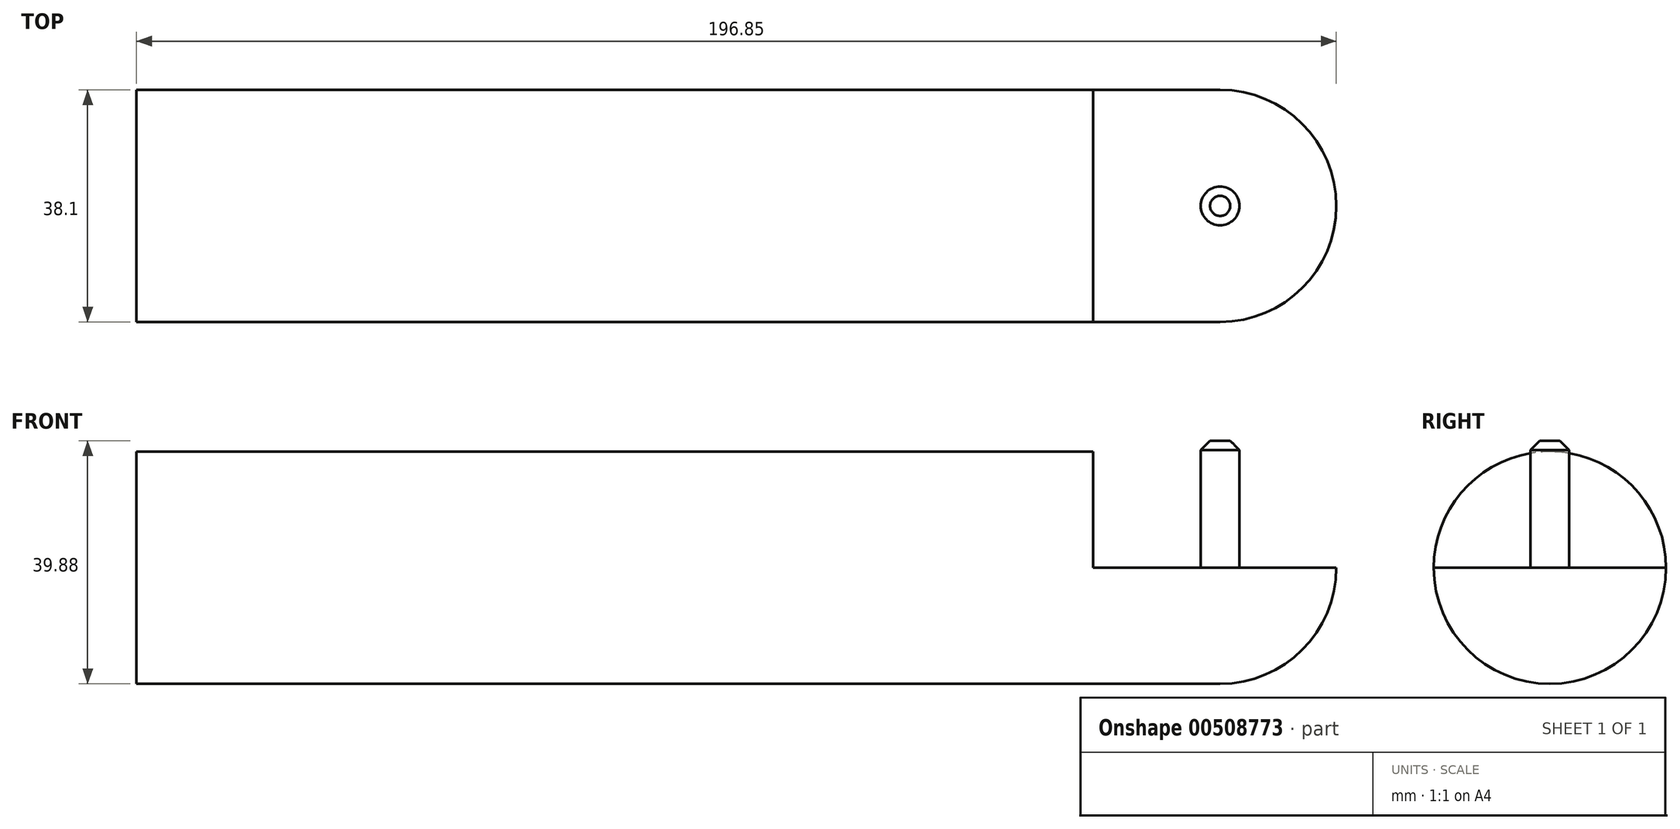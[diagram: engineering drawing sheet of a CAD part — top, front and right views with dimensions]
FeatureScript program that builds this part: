
annotation { "Feature Type Name" : "Feature", "Feature Type Description" : "" }
export const myFeature = defineFeature(function(context is Context, id is Id, definition is map)
    precondition{}
    {
        {
            var Q0;
            Q0=qCreatedBy(makeId("Top.planeOp"),FACE);
            var sketch = newSketch(context, id + "F0", { "sketchPlane" : qUnion([Q0])});
            skLineSegment(sketch, "E0.0", {"start": v(0, -19.05) * mm, "end": v(-177.8, -19.05) * mm});
            skLineSegment(sketch, "E1.0", {"start": v(0, 19.05) * mm, "end": v(-177.8, 19.05) * mm});
            skLineSegment(sketch, "E2", {"start": v(-177.8, 19.05) * mm, "end": v(-177.8, 0) * mm});
            skLineSegment(sketch, "E3", {"start": v(-177.8, -19.05) * mm, "end": v(-177.8, 0) * mm});
            skArc(sketch, "E4", {"start": v(0, 19.05) * mm, "mid": v(19.05, 0) * mm, "end": v(0, -19.05) * mm});
            skLineSegment(sketch, "E5", {"start": v(-177.8, 0) * mm, "end": v(19.05, 0) * mm});
            skSolve(sketch);
        }
        {
            var Q0;
            {var subQ0=sQuery(id+"F0.wireOp",EDGE,"E1.0");Q0=makeQuery(id+"F0.imprint","IMPRINT",FACE,{"disambiguationData":[TD([[makeQuery(id+"F0.imprint","IMPRINT",EDGE,{"derivedFrom":subQ0}),1.0]])]});}
            var Q1;
            Q1=sQuery(id+"F0.wireOp",EDGE,"E5");
            revolve(context, id + "F1", {"entities" : qUnion([Q0]), "axis" : qUnion([Q1]), "revolveType" : RevolveType.FULL});
        }
        {
            var Q0;
            Q0=qCreatedBy(makeId("Top.planeOp"),FACE);
            var sketch = newSketch(context, id + "F2", { "sketchPlane" : qUnion([Q0])});
            skArc(sketch, "E6", {"start": v(0, -19.05) * mm, "mid": v(19.05, 0) * mm, "end": v(0, 19.05) * mm});
            skLineSegment(sketch, "E7", {"start": v(-177.8, 19.05) * mm, "end": v(0, 19.05) * mm});
            skLineSegment(sketch, "E8", {"start": v(0, 0) * mm, "end": v(-20.83, 0) * mm});
            skLineSegment(sketch, "E9", {"start": v(-20.83, 0) * mm, "end": v(-20.83, 19.05) * mm});
            skLineSegment(sketch, "E10", {"start": v(-20.83, 0) * mm, "end": v(-20.83, -19.05) * mm});
            skLineSegment(sketch, "E11", {"start": v(0, -19.05) * mm, "end": v(-177.8, -19.05) * mm});
            skSolve(sketch);
        }
        {
            var Q0;
            Q0=qSketchRegion(id+"F2",true);
            extrude(context, id + "F3", {"entities" : qUnion([Q0]), "operationType" : NewBodyOperationType.REMOVE, "depth" : 25.4 * mm});
        }
        {
            var Q0;
            Q0=makeQuery(id+"F3.boolean.opBoolean","COPY",FACE,{"derivedFrom":makeQuery(id+"F3.opExtrude","CAP_FACE",FACE,{"disambiguationData":[OSD([sQuery(id+"F2.wireOp",EDGE,"E6"),sQuery(id+"F2.wireOp",EDGE,"E7"),sQuery(id+"F2.wireOp",EDGE,"E9"),sQuery(id+"F2.wireOp",EDGE,"E10"),sQuery(id+"F2.wireOp",EDGE,"E11")])],"isStart":true})});
            var sketch = newSketch(context, id + "F4", { "sketchPlane" : qUnion([Q0])});
            skCircle(sketch, "E12", {"center": v(0, 0) * mm, "radius": 3.18 * mm});
            skSolve(sketch);
        }
        {
            var Q0;
            Q0=makeQuery(id+"F4.imprint","IMPRINT",FACE,{"disambiguationData":[TD([[makeQuery(id+"F4.imprint","IMPRINT",EDGE,{"derivedFrom":sQuery(id+"F4.wireOp",EDGE,"E12")}),1.0]])]});
            extrude(context, id + "F5", {"entities" : qUnion([Q0]), "operationType" : NewBodyOperationType.ADD, "depth" : 20.83 * mm});
        }
        {
            var Q0;
            Q0=makeQuery(id+"F5.opExtrude","CAP_FACE",FACE,{"disambiguationData":[OSD([sQuery(id+"F4.wireOp",EDGE,"E12")])],"isStart":false});
            chamfer(context, id + "F6", {"entities" : qUnion([Q0]), "width" : 1.52 * mm, "tangentPropagation" : true});
        }
    });
